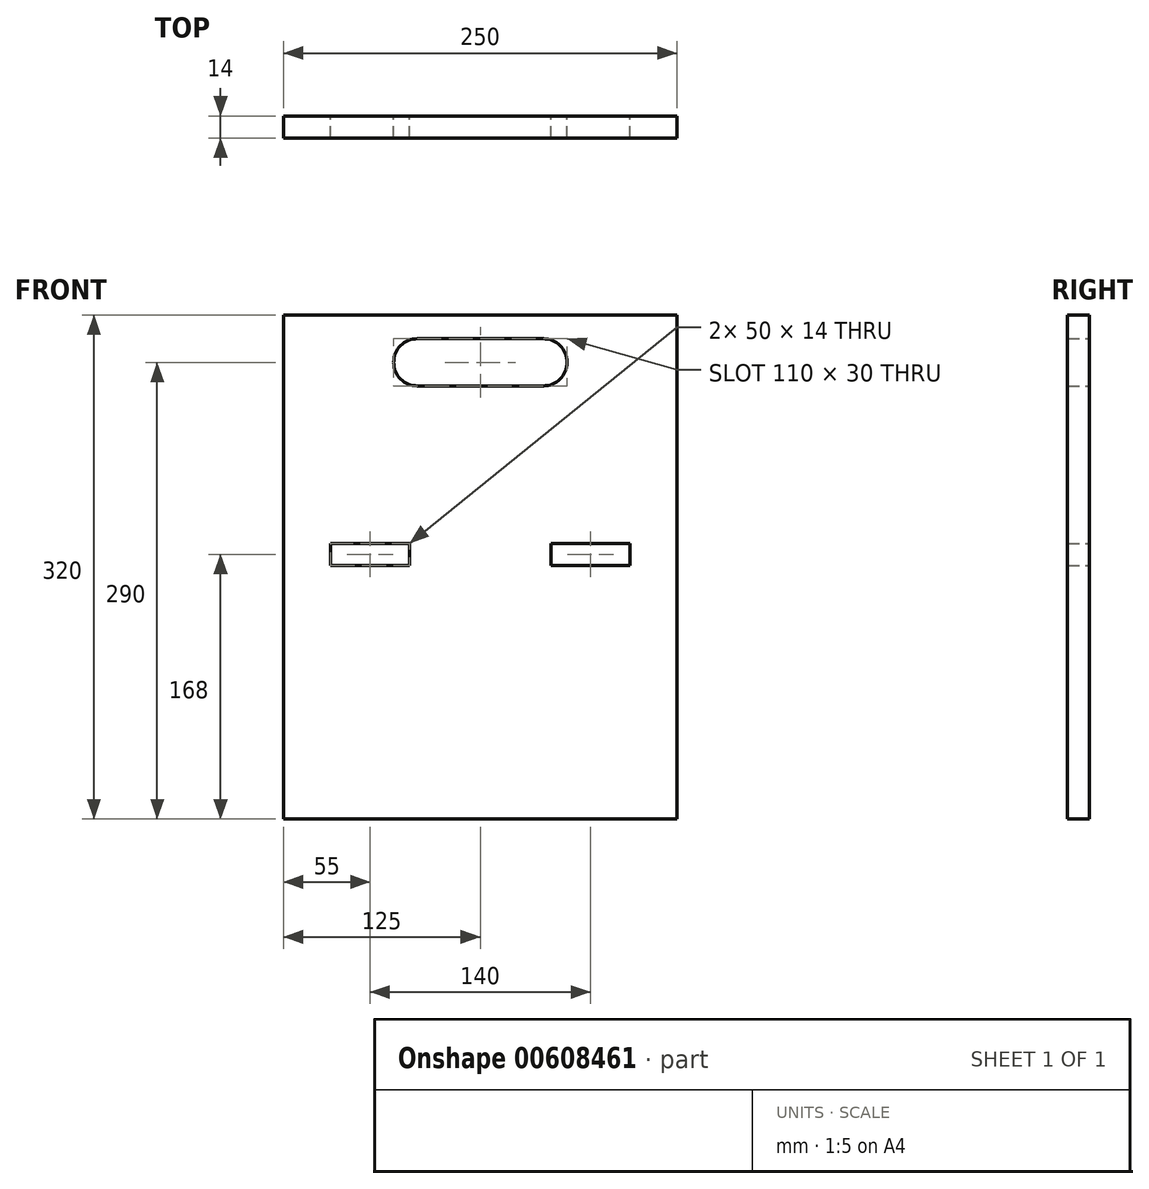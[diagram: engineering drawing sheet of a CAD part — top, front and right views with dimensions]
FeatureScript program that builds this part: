
annotation { "Feature Type Name" : "Feature", "Feature Type Description" : "" }
export const myFeature = defineFeature(function(context is Context, id is Id, definition is map)
    precondition{}
    {
        {
            var Q0;
            Q0=qCreatedBy(makeId("Front.planeOp"),FACE);
            var sketch = newSketch(context, id + "F0", { "sketchPlane" : qUnion([Q0])});
            skLineSegment(sketch, "E0", {"start": v(-125, 0) * mm, "end": v(-125, -175) * mm});
            skLineSegment(sketch, "E1", {"start": v(-125, -175) * mm, "end": v(125, -175) * mm});
            skLineSegment(sketch, "E2", {"start": v(125, -175) * mm, "end": v(125, 0) * mm});
            skLineSegment(sketch, "E3.bottom", {"start": v(-40, 130) * mm, "end": v(40, 130) * mm});
            skLineSegment(sketch, "E3.top", {"start": v(-40, 100) * mm, "end": v(40, 100) * mm});
            skLineSegment(sketch, "E3.left", {"start": v(-55, 115) * mm, "end": v(-55, 115) * mm});
            skLineSegment(sketch, "E3.right", {"start": v(55, 115) * mm, "end": v(55, 115) * mm});
            skPoint(sketch, "E4.visualSharp", {"position": v(-55, 130) * mm});
            skArc(sketch, "E4.filletArc", {"start": v(-40, 130) * mm, "mid": v(-50.6, 125.6) * mm, "end": v(-55, 115) * mm});
            skPoint(sketch, "E5.visualSharp", {"position": v(-55, 100) * mm});
            skArc(sketch, "E5.filletArc", {"start": v(-55, 115) * mm, "mid": v(-50.6, 104.4) * mm, "end": v(-40, 100) * mm});
            skPoint(sketch, "E6.visualSharp", {"position": v(55, 130) * mm});
            skArc(sketch, "E6.filletArc", {"start": v(55, 115) * mm, "mid": v(50.6, 125.6) * mm, "end": v(40, 130) * mm});
            skPoint(sketch, "E7.visualSharp", {"position": v(55, 100) * mm});
            skArc(sketch, "E7.filletArc", {"start": v(40, 100) * mm, "mid": v(50.6, 104.4) * mm, "end": v(55, 115) * mm});
            skLineSegment(sketch, "E8", {"start": v(-40, 115) * mm, "end": v(40, 115) * mm, "construction": true});
            skPoint(sketch, "E9", {"position": v(0, 115) * mm});
            skLineSegment(sketch, "E10.bottom", {"start": v(-95, 0) * mm, "end": v(-45, 0) * mm});
            skLineSegment(sketch, "E10.top", {"start": v(-95, -14) * mm, "end": v(-45, -14) * mm});
            skLineSegment(sketch, "E10.left", {"start": v(-95, 0) * mm, "end": v(-95, -14) * mm});
            skLineSegment(sketch, "E10.right", {"start": v(-45, 0) * mm, "end": v(-45, -14) * mm});
            skLineSegment(sketch, "E11.MirrorCS", {"start": v(95, 0) * mm, "end": v(95, -14) * mm});
            skLineSegment(sketch, "E12.MirrorCS", {"start": v(45, 0) * mm, "end": v(45, -14) * mm});
            skLineSegment(sketch, "E13.MirrorCS", {"start": v(95, 0) * mm, "end": v(45, 0) * mm});
            skLineSegment(sketch, "E14.MirrorCS", {"start": v(95, -14) * mm, "end": v(45, -14) * mm});
            skLineSegment(sketch, "E15", {"start": v(-125, 0) * mm, "end": v(-125, 145) * mm});
            skLineSegment(sketch, "E16", {"start": v(-125, 145) * mm, "end": v(125, 145) * mm});
            skLineSegment(sketch, "E17", {"start": v(125, 145) * mm, "end": v(125, 0) * mm});
            skPoint(sketch, "E18", {"position": v(0, -175) * mm});
            skSolve(sketch);
        }
        {
            var Q0;
            Q0=makeQuery(id+"F0.imprint","IMPRINT",FACE,{"disambiguationData":[TD([[makeQuery(id+"F0.imprint","IMPRINT",EDGE,{"derivedFrom":sQuery(id+"F0.wireOp",EDGE,"E0")}),1.0]])]});
            extrude(context, id + "F1", {"entities" : qUnion([Q0]), "depth" : 14 * mm, "offsetDistance" : 25 * mm});
        }
    });
